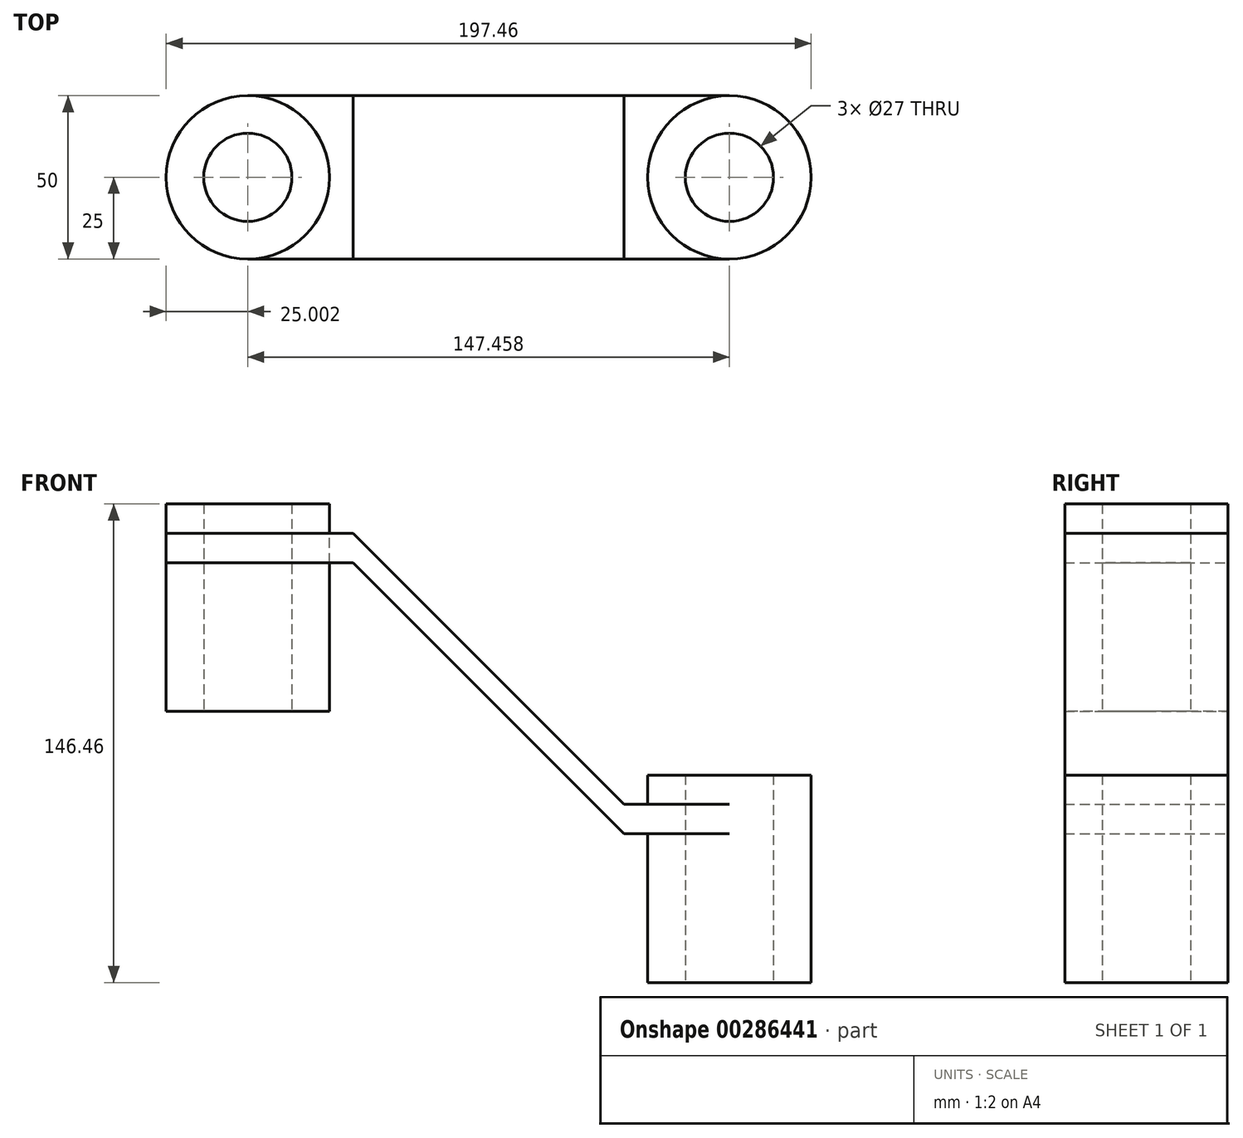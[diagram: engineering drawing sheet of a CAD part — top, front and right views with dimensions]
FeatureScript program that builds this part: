
annotation { "Feature Type Name" : "Feature", "Feature Type Description" : "" }
export const myFeature = defineFeature(function(context is Context, id is Id, definition is map)
    precondition{}
    {
        {
            var Q0;
            Q0=qCreatedBy(makeId("Front.planeOp"),FACE);
            var sketch = newSketch(context, id + "F0", { "sketchPlane" : qUnion([Q0])});
            skLineSegment(sketch, "E0.bottom", {"start": v(0, 0) * mm, "end": v(-64.5, 0) * mm});
            skLineSegment(sketch, "E0.top", {"start": v(0, 9) * mm, "end": v(-64.5, 9) * mm});
            skLineSegment(sketch, "E0.left", {"start": v(0, 0) * mm, "end": v(0, 9) * mm});
            skLineSegment(sketch, "E1", {"start": v(-64.5, 9) * mm, "end": v(-147.46, 91.96) * mm});
            skLineSegment(sketch, "E2", {"start": v(-64.5, 0) * mm, "end": v(-147.46, 82.96) * mm});
            skLineSegment(sketch, "E3.bottom", {"start": v(-147.46, 82.96) * mm, "end": v(-211.96, 82.96) * mm});
            skLineSegment(sketch, "E3.top", {"start": v(-147.46, 91.96) * mm, "end": v(-211.96, 91.96) * mm});
            skLineSegment(sketch, "E3.right", {"start": v(-211.96, 82.96) * mm, "end": v(-211.96, 91.96) * mm});
            skSolve(sketch);
        }
        {
            var Q0;
            Q0=sQuery(id+"F0.wireOp",EDGE,"E3.bottom");
            var Q1;
            Q1=sQuery(id+"F0.wireOp",EDGE,"E3.top");
            var Q2;
            Q2=sQuery(id+"F0.wireOp",EDGE,"E3.right");
            var Q3;
            Q3=sQuery(id+"F0.wireOp",EDGE,"E1");
            var Q4;
            Q4=sQuery(id+"F0.wireOp",EDGE,"E2");
            var Q5;
            Q5=sQuery(id+"F0.wireOp",EDGE,"E0.bottom");
            var Q6;
            Q6=sQuery(id+"F0.wireOp",EDGE,"E0.top");
            var Q7;
            Q7=sQuery(id+"F0.wireOp",EDGE,"E0.left");
            extrude(context, id + "F1", {"bodyType" : ToolBodyType.SURFACE, "surfaceEntities" : qUnion([Q0, Q1, Q2, Q3, Q4, Q5, Q6, Q7]), "depth" : 50 * mm});
        }
        {
            var Q0;
            Q0=makeQuery(id+"F0.imprint","IMPRINT",FACE,{"disambiguationData":[TD([[makeQuery(id+"F0.imprint","IMPRINT",EDGE,{"derivedFrom":sQuery(id+"F0.wireOp",EDGE,"E0.bottom")}),-1.0]])]});
            extrude(context, id + "F2", {"entities" : qUnion([Q0]), "depth" : 2 * 25 * mm});
        }
        {
            var Q0;
            Q0=makeQuery(id+"F1.opExtrude","SWEPT_FACE",FACE,{"disambiguationData":[OSD([sQuery(id+"F0.wireOp",EDGE,"E0.bottom")])]});
            var sketch = newSketch(context, id + "F3", { "sketchPlane" : qUnion([Q0])});
            skCircle(sketch, "E4", {"center": v(-32.25, -25) * mm, "radius": 25 * mm});
            skCircle(sketch, "E5", {"center": v(-180.28, -25) * mm, "radius": 25 * mm});
            skSolve(sketch);
        }
        {
            var Q0;
            {var subQ0=sQuery(id+"F3.wireOp",EDGE,"E4");var subQ1=sQuery(id+"F0.wireOp",EDGE,"E0.bottom");var subQ2=makeQuery(id+"F3.imprint","INTERSECT",VERTEX,{"derivedFrom":[makeQuery(id+"F1.opExtrude","CAP_EDGE",EDGE,{"disambiguationData":[OSD([subQ1])],"isStart":true}),subQ0]});Q0=makeQuery(id+"F3.imprint","IMPRINT",FACE,{"disambiguationData":[TD([[makeQuery(id+"F3.imprint","IMPRINT",EDGE,{"disambiguationData":[TD([[subQ2,-1.0]])],"derivedFrom":subQ0}),1.0]])]});}
            extrude(context, id + "F4", {"entities" : qUnion([Q0]), "operationType" : NewBodyOperationType.ADD, "oppositeDirection" : true, "depth" : 45.5 * mm, "hasSecondDirection" : true, "secondDirectionOppositeDirection" : false, "secondDirectionDepth" : 18 * mm});
        }
        {
            var Q0;
            Q0=makeQuery(id+"F1.opExtrude","SWEPT_FACE",FACE,{"disambiguationData":[OSD([sQuery(id+"F0.wireOp",EDGE,"E3.bottom")])]});
            var sketch = newSketch(context, id + "F5", { "sketchPlane" : qUnion([Q0])});
            skCircle(sketch, "E6", {"center": v(-179.7, -25) * mm, "radius": 25 * mm});
            skSolve(sketch);
        }
        {
            var Q0;
            {var subQ0=sQuery(id+"F5.wireOp",EDGE,"E6");var subQ1=sQuery(id+"F0.wireOp",EDGE,"E3.bottom");var subQ2=makeQuery(id+"F5.imprint","INTERSECT",VERTEX,{"derivedFrom":[makeQuery(id+"F1.opExtrude","CAP_EDGE",EDGE,{"disambiguationData":[OSD([subQ1])],"isStart":true}),subQ0]});Q0=makeQuery(id+"F5.imprint","IMPRINT",FACE,{"disambiguationData":[TD([[makeQuery(id+"F5.imprint","IMPRINT",EDGE,{"disambiguationData":[TD([[subQ2,-1.0]])],"derivedFrom":subQ0}),1.0]])]});}
            extrude(context, id + "F6", {"entities" : qUnion([Q0]), "oppositeDirection" : true, "depth" : 45.5 * mm, "hasSecondDirection" : true, "secondDirectionOppositeDirection" : false, "secondDirectionDepth" : 18 * mm});
        }
        {
            var Q0;
            Q0=makeQuery(id+"F6.opExtrude","CAP_FACE",FACE,{"disambiguationData":[OSD([sQuery(id+"F5.wireOp",EDGE,"E6")])],"isStart":false});
            var sketch = newSketch(context, id + "F7", { "sketchPlane" : qUnion([Q0])});
            skCircle(sketch, "E7", {"center": v(-179.7, 25) * mm, "radius": 13.5 * mm});
            skSolve(sketch);
        }
        {
            var Q0;
            Q0=makeQuery(id+"F4.opExtrude","CAP_FACE",FACE,{"disambiguationData":[OSD([sQuery(id+"F3.wireOp",EDGE,"E4")])],"isStart":false});
            var sketch = newSketch(context, id + "F8", { "sketchPlane" : qUnion([Q0])});
            skCircle(sketch, "E8", {"center": v(-32.25, 25) * mm, "radius": 13.5 * mm});
            skSolve(sketch);
        }
        {
            var Q0;
            Q0=makeQuery(id+"F8.imprint","IMPRINT",FACE,{"disambiguationData":[TD([[makeQuery(id+"F8.imprint","IMPRINT",EDGE,{"derivedFrom":sQuery(id+"F8.wireOp",EDGE,"E8")}),1.0]])]});
            var Q1;
            Q1=makeQuery(id+"F7.imprint","IMPRINT",FACE,{"disambiguationData":[TD([[makeQuery(id+"F7.imprint","IMPRINT",EDGE,{"derivedFrom":sQuery(id+"F7.wireOp",EDGE,"E7")}),1.0]])]});
            extrude(context, id + "F9", {"entities" : qUnion([Q0, Q1]), "operationType" : NewBodyOperationType.REMOVE, "oppositeDirection" : true, "depth" : 87 * mm});
        }
        {
            var Q0;
            Q0=makeQuery(id+"F8.imprint","IMPRINT",FACE,{"disambiguationData":[TD([[makeQuery(id+"F8.imprint","IMPRINT",EDGE,{"derivedFrom":sQuery(id+"F8.wireOp",EDGE,"E8")}),1.0]])]});
            extrude(context, id + "F10", {"entities" : qUnion([Q0]), "operationType" : NewBodyOperationType.REMOVE, "oppositeDirection" : true, "depth" : 200 * mm});
        }
        {
            var Q0;
            Q0=makeQuery(id+"F7.imprint","IMPRINT",FACE,{"disambiguationData":[TD([[makeQuery(id+"F7.imprint","IMPRINT",EDGE,{"derivedFrom":sQuery(id+"F7.wireOp",EDGE,"E7")}),1.0]])]});
            extrude(context, id + "F11", {"entities" : qUnion([Q0]), "operationType" : NewBodyOperationType.REMOVE, "oppositeDirection" : true, "depth" : 100 * mm});
        }
        {
            var Q0;
            Q0=makeQuery(id+"F1.opExtrude","SWEPT_FACE",FACE,{"disambiguationData":[OSD([sQuery(id+"F0.wireOp",EDGE,"E0.bottom")])]});
            var sketch = newSketch(context, id + "F12", { "sketchPlane" : qUnion([Q0])});
            skCircle(sketch, "E9.0", {"center": v(-32.25, -25) * mm, "radius": 25 * mm});
            skCircle(sketch, "E10.1", {"center": v(-179.7, -25) * mm, "radius": 25 * mm});
            skLineSegment(sketch, "E10.2", {"start": v(-211.96, 0) * mm, "end": v(-211.96, -50) * mm});
            skLineSegment(sketch, "E10.3", {"start": v(-211.96, -50) * mm, "end": v(-147.46, -50) * mm});
            skLineSegment(sketch, "E10.4", {"start": v(-147.46, 0) * mm, "end": v(-211.96, 0) * mm});
            skSolve(sketch);
        }
        {
            var Q0;
            {var subQ5=sQuery(id+"F12.wireOp",EDGE,"E10.2");Q0=makeQuery(id+"F12.imprint","IMPRINT",FACE,{"disambiguationData":[TD([[makeQuery(id+"F12.imprint","IMPRINT",EDGE,{"derivedFrom":subQ5}),1.0]])]});}
            var Q1;
            {var subQ6=makeQuery(id+"F1.opExtrude","SWEPT_EDGE",EDGE,{"disambiguationData":[OSD([sQuery(id+"F0.wireOp",VERTEX,"E0.left.start")])]});Q1=makeQuery(id+"F12.imprint","IMPRINT",FACE,{"disambiguationData":[TD([[makeQuery(id+"F12.imprint","IMPRINT",EDGE,{"derivedFrom":subQ6}),-1.0]])]});}
            extrude(context, id + "F13", {"entities" : qUnion([Q0, Q1]), "operationType" : NewBodyOperationType.REMOVE, "depth" : 150 * mm});
        }
    });
